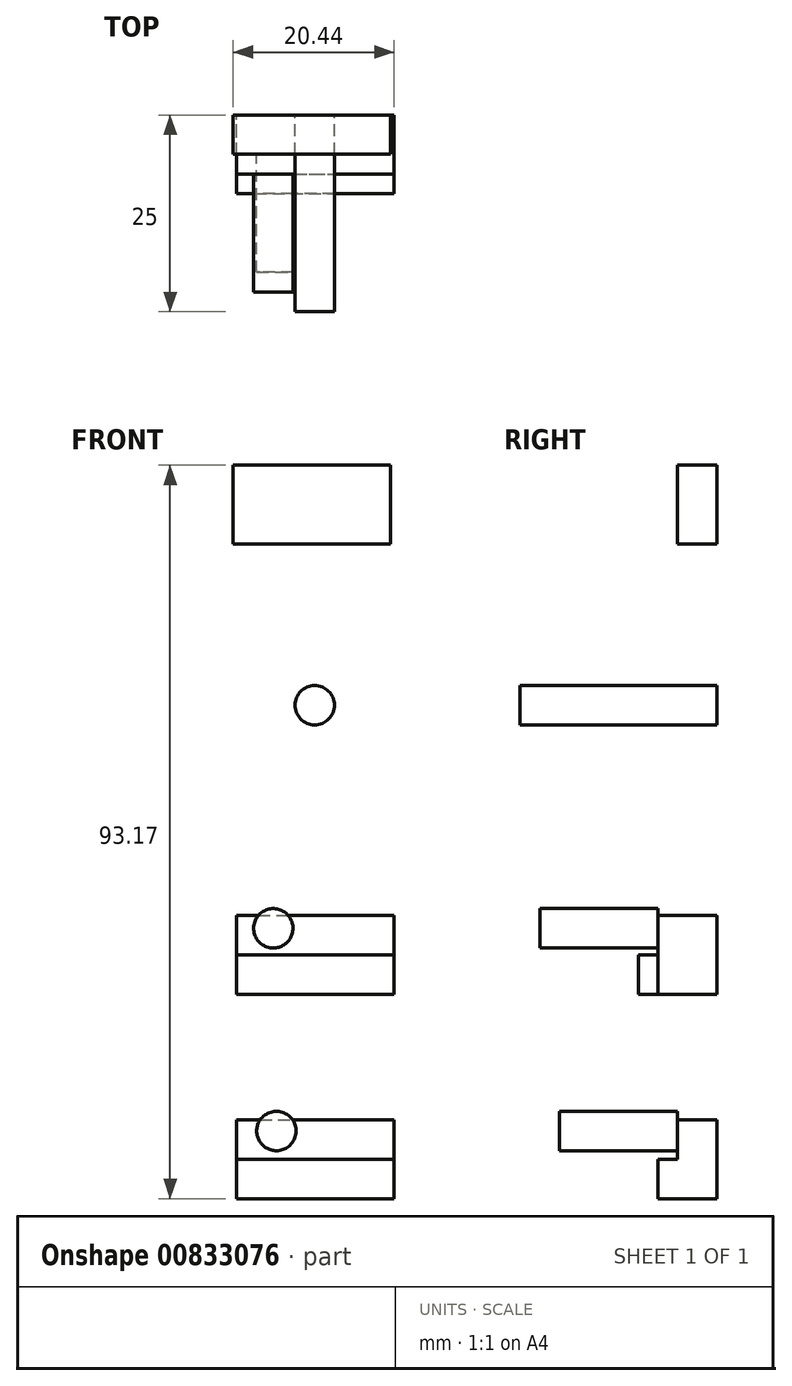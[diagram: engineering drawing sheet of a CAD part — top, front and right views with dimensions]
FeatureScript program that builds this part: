
annotation { "Feature Type Name" : "Feature", "Feature Type Description" : "" }
export const myFeature = defineFeature(function(context is Context, id is Id, definition is map)
    precondition{}
    {
        {
            var Q0;
            Q0=qCreatedBy(makeId("Front.planeOp"),FACE);
            var sketch = newSketch(context, id + "F0", { "sketchPlane" : qUnion([Q0])});
            skLineSegment(sketch, "E0.bottom", {"start": v(-10.44, 33.98) * mm, "end": v(9.56, 33.98) * mm});
            skLineSegment(sketch, "E0.top", {"start": v(-10.44, 23.98) * mm, "end": v(9.56, 23.98) * mm});
            skLineSegment(sketch, "E0.left", {"start": v(-10.44, 33.98) * mm, "end": v(-10.44, 23.98) * mm});
            skLineSegment(sketch, "E0.right", {"start": v(9.56, 33.98) * mm, "end": v(9.56, 23.98) * mm});
            skLineSegment(sketch, "E1.MirrorCS", {"start": v(10.44, 33.98) * mm, "end": v(10.44, 23.98) * mm});
            skLineSegment(sketch, "E2.MirrorCS", {"start": v(10.44, 33.98) * mm, "end": v(-9.56, 33.98) * mm});
            skLineSegment(sketch, "E3.MirrorCS", {"start": v(10.44, 23.98) * mm, "end": v(-9.56, 23.98) * mm});
            skSolve(sketch);
        }
        {
            var Q0;
            {var subQ2=sQuery(id+"F0.wireOp",EDGE,"E0.left");Q0=makeQuery(id+"F0.imprint","IMPRINT",FACE,{"disambiguationData":[TD([[makeQuery(id+"F0.imprint","IMPRINT",EDGE,{"derivedFrom":subQ2}),1.0]])]});}
            extrude(context, id + "F1", {"entities" : qUnion([Q0]), "depth" : 5 * mm, "offsetDistance" : 25 * mm});
        }
        {
            var Q0;
            Q0=qCreatedBy(makeId("Front.planeOp"),FACE);
            var sketch = newSketch(context, id + "F2", { "sketchPlane" : qUnion([Q0])});
            skCircle(sketch, "E4", {"center": v(-0.1, 3.49) * mm, "radius": 2.5 * mm});
            skSolve(sketch);
        }
        {
            var Q0;
            Q0=makeQuery(id+"F2.imprint","IMPRINT",FACE,{"disambiguationData":[TD([[makeQuery(id+"F2.imprint","IMPRINT",EDGE,{"derivedFrom":sQuery(id+"F2.wireOp",EDGE,"E4")}),1.0]])]});
            extrude(context, id + "F3", {"entities" : qUnion([Q0]), "depth" : 25 * mm, "offsetDistance" : 25 * mm});
        }
        {
            var Q0;
            Q0=qCreatedBy(makeId("Front.planeOp"),FACE);
            var sketch = newSketch(context, id + "F4", { "sketchPlane" : qUnion([Q0])});
            skLineSegment(sketch, "E5.bottom", {"start": v(-10, -23.23) * mm, "end": v(10, -23.23) * mm});
            skLineSegment(sketch, "E5.top", {"start": v(-10, -33.23) * mm, "end": v(10, -33.23) * mm});
            skLineSegment(sketch, "E5.left", {"start": v(-10, -23.23) * mm, "end": v(-10, -33.23) * mm});
            skLineSegment(sketch, "E5.right", {"start": v(10, -23.23) * mm, "end": v(10, -33.23) * mm});
            skLineSegment(sketch, "E6.MirrorCS", {"start": v(12.96, -23.23) * mm, "end": v(-7.04, -23.23) * mm});
            skLineSegment(sketch, "E7.MirrorCS", {"start": v(12.96, -33.23) * mm, "end": v(-7.04, -33.23) * mm});
            skSolve(sketch);
        }
        {
            var Q0;
            {var subQ2=sQuery(id+"F4.wireOp",EDGE,"E5.left");Q0=makeQuery(id+"F4.imprint","IMPRINT",FACE,{"disambiguationData":[TD([[makeQuery(id+"F4.imprint","IMPRINT",EDGE,{"derivedFrom":subQ2}),1.0]])]});}
            extrude(context, id + "F5", {"entities" : qUnion([Q0]), "depth" : 7.5 * mm, "offsetDistance" : 25 * mm});
        }
        {
            var Q0;
            Q0=qCreatedBy(makeId("Front.planeOp"),FACE);
            var sketch = newSketch(context, id + "F6", { "sketchPlane" : qUnion([Q0])});
            skLineSegment(sketch, "E8.bottom", {"start": v(-10, -49.2) * mm, "end": v(10, -49.2) * mm});
            skLineSegment(sketch, "E8.top", {"start": v(-10, -59.2) * mm, "end": v(10, -59.2) * mm});
            skLineSegment(sketch, "E8.left", {"start": v(-10, -49.2) * mm, "end": v(-10, -59.2) * mm});
            skLineSegment(sketch, "E8.right", {"start": v(10, -49.2) * mm, "end": v(10, -59.2) * mm});
            skLineSegment(sketch, "E9.MirrorCS", {"start": v(7.26, -49.2) * mm, "end": v(-12.74, -49.2) * mm});
            skLineSegment(sketch, "E10.MirrorCS", {"start": v(7.26, -59.2) * mm, "end": v(-12.74, -59.2) * mm});
            skSolve(sketch);
        }
        {
            var Q0;
            {var subQ3=sQuery(id+"F6.wireOp",EDGE,"E8.bottom");Q0=makeQuery(id+"F6.imprint","IMPRINT",FACE,{"disambiguationData":[TD([[makeQuery(id+"F6.imprint","IMPRINT",EDGE,{"derivedFrom":subQ3}),-1.0]])]});}
            extrude(context, id + "F7", {"entities" : qUnion([Q0]), "depth" : 5 * mm, "offsetDistance" : 25 * mm});
        }
        {
            var Q0;
            Q0=makeQuery(id+"F5.opExtrude","CAP_FACE",FACE,{"disambiguationData":[OSD([sQuery(id+"F4.wireOp",EDGE,"E5.bottom"),sQuery(id+"F4.wireOp",EDGE,"E5.top"),sQuery(id+"F4.wireOp",EDGE,"E5.left"),sQuery(id+"F4.wireOp",EDGE,"E5.right")])],"isStart":false});
            var sketch = newSketch(context, id + "F8", { "sketchPlane" : qUnion([Q0])});
            skLineSegment(sketch, "E11.bottom", {"start": v(10, -28.23) * mm, "end": v(-10, -28.23) * mm});
            skLineSegment(sketch, "E11.top", {"start": v(10, -33.23) * mm, "end": v(-10, -33.23) * mm});
            skLineSegment(sketch, "E11.left", {"start": v(10, -28.23) * mm, "end": v(10, -33.23) * mm});
            skLineSegment(sketch, "E11.right", {"start": v(-10, -28.23) * mm, "end": v(-10, -33.23) * mm});
            skCircle(sketch, "E12", {"center": v(-3.98, -24.01) * mm, "radius": 2.5 * mm});
            skSolve(sketch);
        }
        {
            var Q0;
            Q0=makeQuery(id+"F8.imprint","IMPRINT",FACE,{"disambiguationData":[TD([[makeQuery(id+"F8.imprint","IMPRINT",EDGE,{"derivedFrom":sQuery(id+"F8.wireOp",EDGE,"E11.bottom")}),1.0]])]});
            extrude(context, id + "F9", {"entities" : qUnion([Q0]), "depth" : 2.5 * mm, "offsetDistance" : 25 * mm});
        }
        {
            var Q0;
            Q0=makeQuery(id+"F7.opExtrude","CAP_FACE",FACE,{"disambiguationData":[OSD([sQuery(id+"F6.wireOp",EDGE,"E8.bottom"),sQuery(id+"F6.wireOp",EDGE,"E8.top"),sQuery(id+"F6.wireOp",EDGE,"E8.right"),sQuery(id+"F6.wireOp",EDGE,"E9.MirrorCS"),sQuery(id+"F6.wireOp",EDGE,"E8.left"),sQuery(id+"F6.wireOp",EDGE,"E10.MirrorCS")])],"isStart":false});
            var sketch = newSketch(context, id + "F10", { "sketchPlane" : qUnion([Q0])});
            skLineSegment(sketch, "E13.bottom", {"start": v(10, -54.2) * mm, "end": v(-10, -54.2) * mm});
            skLineSegment(sketch, "E13.top", {"start": v(10, -59.2) * mm, "end": v(-10, -59.2) * mm});
            skLineSegment(sketch, "E13.left", {"start": v(10, -54.2) * mm, "end": v(10, -59.2) * mm});
            skLineSegment(sketch, "E13.right", {"start": v(-10, -54.2) * mm, "end": v(-10, -59.2) * mm});
            skSolve(sketch);
        }
        {
            var Q0;
            Q0=makeQuery(id+"F10.imprint","IMPRINT",FACE,{"disambiguationData":[TD([[makeQuery(id+"F10.imprint","IMPRINT",EDGE,{"derivedFrom":sQuery(id+"F10.wireOp",EDGE,"E13.bottom")}),1.0]])]});
            extrude(context, id + "F11", {"entities" : qUnion([Q0]), "operationType" : NewBodyOperationType.ADD, "depth" : 2.5 * mm, "offsetDistance" : 25 * mm});
        }
        {
            var Q0;
            Q0=makeQuery(id+"F5.opExtrude","CAP_FACE",FACE,{"disambiguationData":[OSD([sQuery(id+"F4.wireOp",EDGE,"E5.bottom"),sQuery(id+"F4.wireOp",EDGE,"E5.top"),sQuery(id+"F4.wireOp",EDGE,"E5.left"),sQuery(id+"F4.wireOp",EDGE,"E5.right")])],"isStart":false});
            var sketch = newSketch(context, id + "F12", { "sketchPlane" : qUnion([Q0])});
            skCircle(sketch, "E14", {"center": v(-5.35, -24.85) * mm, "radius": 2.5 * mm});
            skSolve(sketch);
        }
        {
            var Q0;
            Q0=makeQuery(id+"F12.imprint","IMPRINT",FACE,{"disambiguationData":[TD([[makeQuery(id+"F12.imprint","IMPRINT",EDGE,{"derivedFrom":sQuery(id+"F12.wireOp",EDGE,"E14")}),1.0]])]});
            extrude(context, id + "F13", {"entities" : qUnion([Q0]), "operationType" : NewBodyOperationType.ADD, "depth" : 15 * mm, "offsetDistance" : 25 * mm});
        }
        {
            var Q0;
            Q0=makeQuery(id+"F7.opExtrude","CAP_FACE",FACE,{"disambiguationData":[OSD([sQuery(id+"F6.wireOp",EDGE,"E8.bottom"),sQuery(id+"F6.wireOp",EDGE,"E8.top"),sQuery(id+"F6.wireOp",EDGE,"E8.right"),sQuery(id+"F6.wireOp",EDGE,"E9.MirrorCS"),sQuery(id+"F6.wireOp",EDGE,"E8.left"),sQuery(id+"F6.wireOp",EDGE,"E10.MirrorCS")])],"isStart":false});
            var sketch = newSketch(context, id + "F14", { "sketchPlane" : qUnion([Q0])});
            skCircle(sketch, "E15", {"center": v(-4.96, -50.6) * mm, "radius": 2.5 * mm});
            skSolve(sketch);
        }
        {
            var Q0;
            {var subQ0=sQuery(id+"F14.wireOp",EDGE,"E15");var subQ1=makeQuery(id+"F7.opExtrude","CAP_EDGE",EDGE,{"disambiguationData":[OSD([sQuery(id+"F6.wireOp",EDGE,"E8.bottom"),sQuery(id+"F6.wireOp",EDGE,"E9.MirrorCS")])],"isStart":false});var subQ2=makeQuery(id+"F14.imprint","INTERSECT",VERTEX,{"disambiguationData":[OD(0.0)],"derivedFrom":[subQ1,subQ0]});Q0=makeQuery(id+"F14.imprint","IMPRINT",FACE,{"disambiguationData":[TD([[makeQuery(id+"F14.imprint","IMPRINT",EDGE,{"disambiguationData":[TD([[subQ2,1.0]])],"derivedFrom":subQ0}),1.0]])]});}
            var Q1;
            {var subQ0=sQuery(id+"F14.wireOp",EDGE,"E15");var subQ1=makeQuery(id+"F7.opExtrude","CAP_EDGE",EDGE,{"disambiguationData":[OSD([sQuery(id+"F6.wireOp",EDGE,"E8.bottom"),sQuery(id+"F6.wireOp",EDGE,"E9.MirrorCS")])],"isStart":false});var subQ2=makeQuery(id+"F14.imprint","INTERSECT",VERTEX,{"disambiguationData":[OD(0.0)],"derivedFrom":[subQ1,subQ0]});Q1=makeQuery(id+"F14.imprint","IMPRINT",FACE,{"disambiguationData":[TD([[makeQuery(id+"F14.imprint","IMPRINT",EDGE,{"disambiguationData":[TD([[subQ2,-1.0]])],"derivedFrom":subQ0}),1.0]])]});}
            extrude(context, id + "F15", {"entities" : qUnion([Q0, Q1]), "operationType" : NewBodyOperationType.ADD, "depth" : 15 * mm, "offsetDistance" : 25 * mm});
        }
    });
